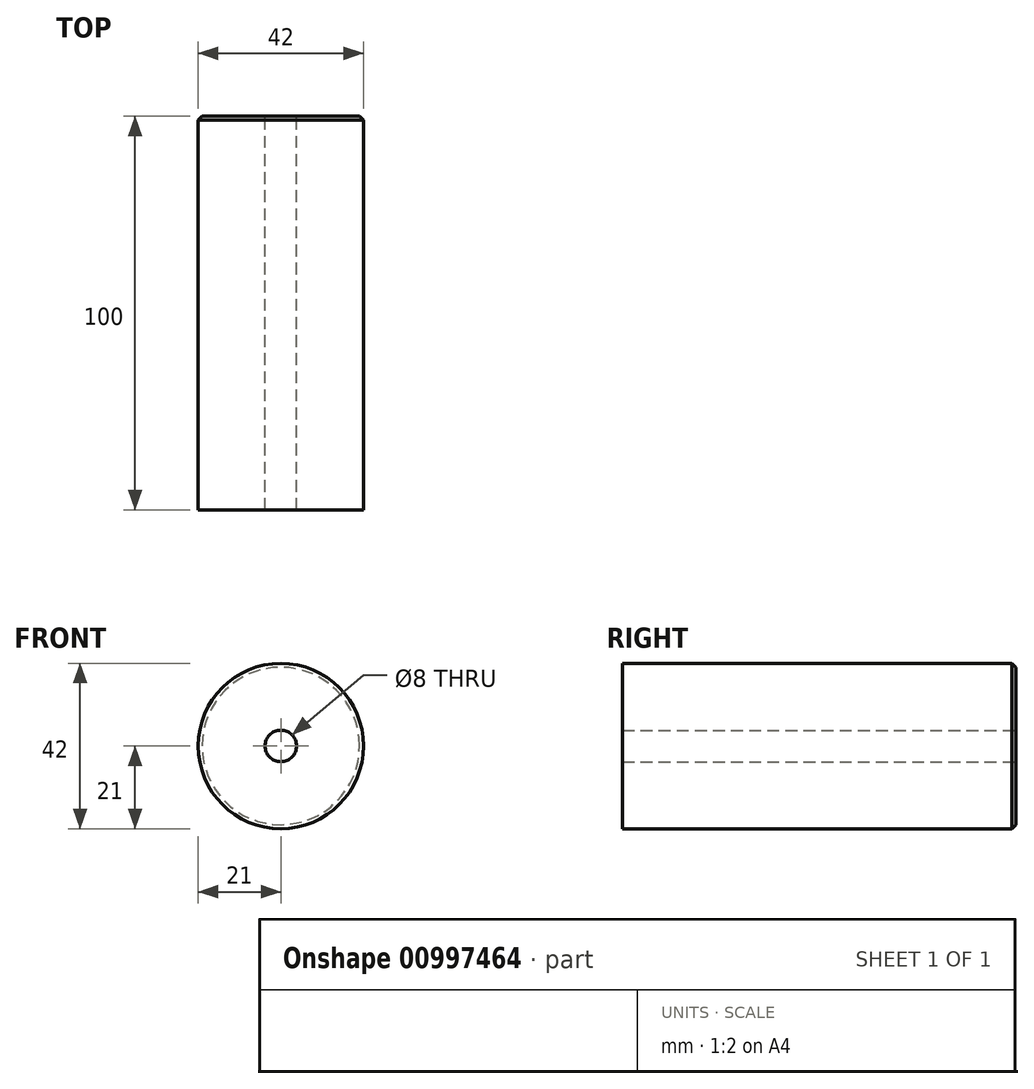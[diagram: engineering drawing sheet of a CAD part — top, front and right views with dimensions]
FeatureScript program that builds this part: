
annotation { "Feature Type Name" : "Feature", "Feature Type Description" : "" }
export const myFeature = defineFeature(function(context is Context, id is Id, definition is map)
    precondition{}
    {
        {
            var Q0;
            Q0=qCreatedBy(makeId("Front.planeOp"),FACE);
            var sketch = newSketch(context, id + "F0", { "sketchPlane" : qUnion([Q0])});
            skCircle(sketch, "E0", {"center": v(0, 0) * mm, "radius": 21 * mm});
            skSolve(sketch);
        }
        {
            var Q0;
            Q0=makeQuery(id+"F0.imprint","IMPRINT",FACE,{"disambiguationData":[TD([[makeQuery(id+"F0.imprint","IMPRINT",EDGE,{"derivedFrom":sQuery(id+"F0.wireOp",EDGE,"E0")}),1.0]])]});
            extrude(context, id + "F1", {"entities" : qUnion([Q0]), "depth" : 100 * mm, "offsetDistance" : 25 * mm});
        }
        {
            var Q0;
            Q0=makeQuery(id+"F1.opExtrude","CAP_EDGE",EDGE,{"disambiguationData":[OSD([sQuery(id+"F0.wireOp",EDGE,"E0")])],"isStart":true});
            chamfer(context, id + "F2", {"entities" : qUnion([Q0]), "width" : 1 * mm, "tangentPropagation" : true});
        }
        {
            var Q0;
            Q0=makeQuery(id+"F1.opExtrude","CAP_FACE",FACE,{"disambiguationData":[OSD([sQuery(id+"F0.wireOp",EDGE,"E0")])],"isStart":true});
            var sketch = newSketch(context, id + "F3", { "sketchPlane" : qUnion([Q0])});
            skCircle(sketch, "E1", {"center": v(0, 0) * mm, "radius": 4 * mm});
            skSolve(sketch);
        }
        {
            var Q0;
            Q0=makeQuery(id+"F3.imprint","IMPRINT",FACE,{"disambiguationData":[TD([[makeQuery(id+"F3.imprint","IMPRINT",EDGE,{"derivedFrom":sQuery(id+"F3.wireOp",EDGE,"E1")}),1.0]])]});
            extrude(context, id + "F4", {"entities" : qUnion([Q0]), "operationType" : NewBodyOperationType.REMOVE, "endBound" : BoundingType.THROUGH_ALL, "oppositeDirection" : true, "depth" : 25 * mm, "offsetDistance" : 25 * mm});
        }
    });
